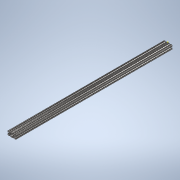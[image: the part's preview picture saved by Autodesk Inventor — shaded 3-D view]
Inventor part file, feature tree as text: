
AUTODESK INVENTOR PART (.ipt)
format: ipt  version: 2020 (Build 240168000, 168)  size: 363,520 bytes
history: native  units: in
note: dims shown in document units (in); Inventor stores cm internally (conversion verified against a paired STEP export)
features: sketch x2, extrude x1
ambient origin geometry x8: Origin, YZ Plane, XZ Plane, XY Plane, X Axis, Y Axis, Z Axis, Center Point
bodies: Solid1 (feature_tree)
feature tree (3):
  extrude  "Extrusion1"  [1 undecoded]
  sketch  "Sketch2"
  sketch  "Sketch1"  dims[d0=38.0in d1=0.0in]
note: 1 required parameter value undecoded (feature->parameter linkage not recoverable at this tier; creation-order binding heuristic only, values carry confidence <= 0.55)
